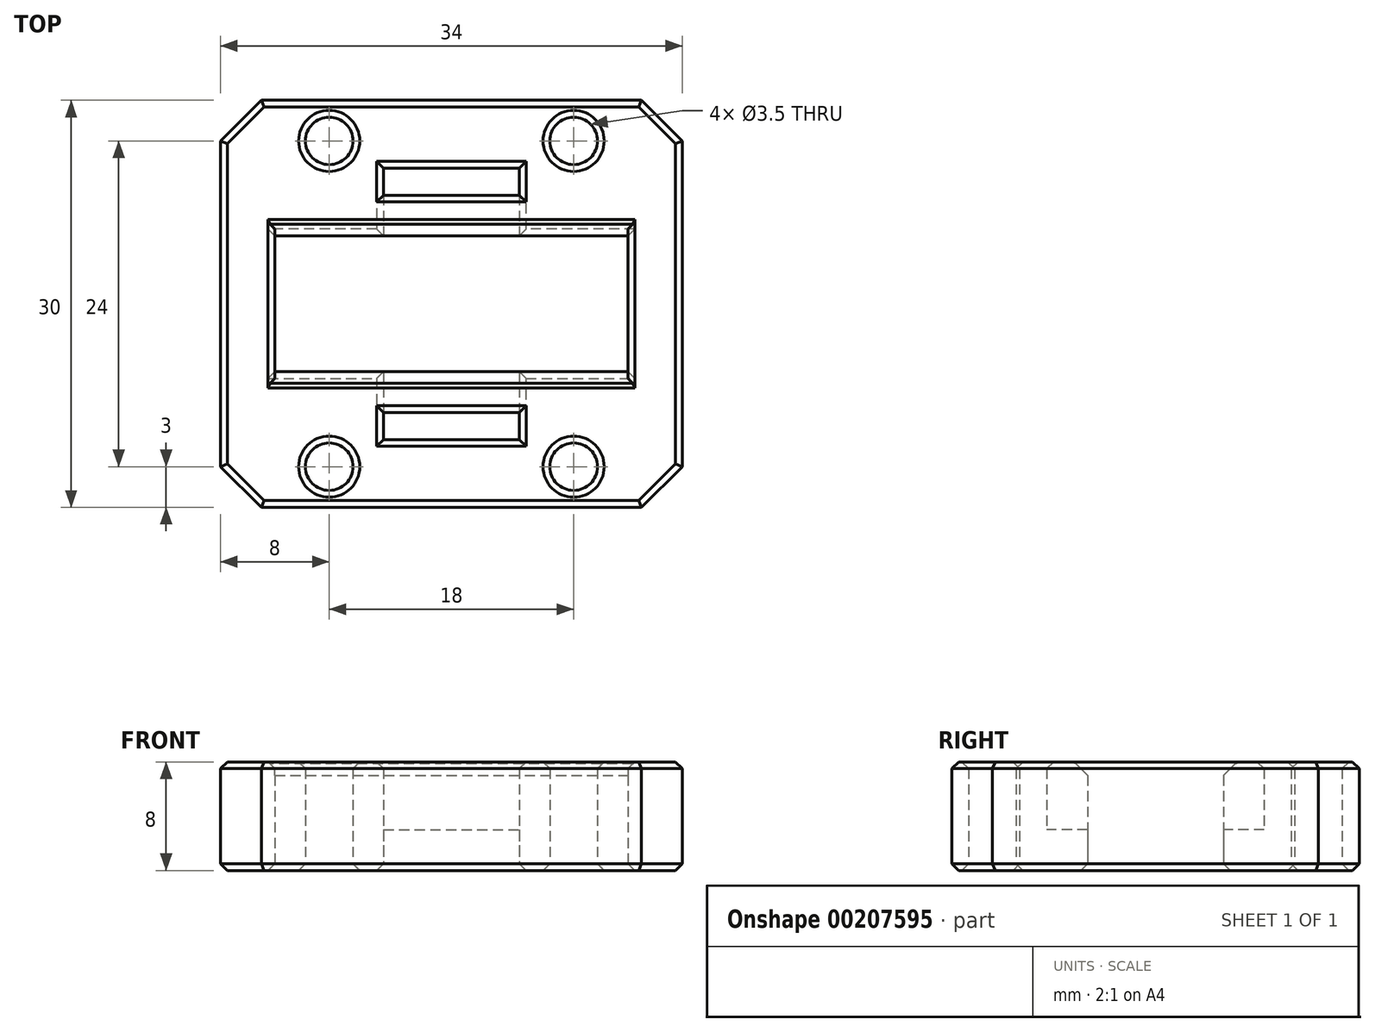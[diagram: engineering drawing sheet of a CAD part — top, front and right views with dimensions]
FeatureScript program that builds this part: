
annotation { "Feature Type Name" : "Feature", "Feature Type Description" : "" }
export const myFeature = defineFeature(function(context is Context, id is Id, definition is map)
    precondition{}
    {
        {
            var Q0;
            Q0=qCreatedBy(makeId("Top.planeOp"),FACE);
            var sketch = newSketch(context, id + "F0", { "sketchPlane" : qUnion([Q0])});
            skLineSegment(sketch, "E0.bottom", {"start": v(-17, 15) * mm, "end": v(17, 15) * mm});
            skLineSegment(sketch, "E0.top", {"start": v(-17, -15) * mm, "end": v(17, -15) * mm});
            skLineSegment(sketch, "E0.left", {"start": v(-17, 15) * mm, "end": v(-17, -15) * mm});
            skLineSegment(sketch, "E0.right", {"start": v(17, 15) * mm, "end": v(17, -15) * mm});
            skCircle(sketch, "E1", {"center": v(-9, 12) * mm, "radius": 1.75 * mm});
            skCircle(sketch, "E2", {"center": v(9, 12) * mm, "radius": 1.75 * mm});
            skCircle(sketch, "E3.MirrorC", {"center": v(-9, -12) * mm, "radius": 1.75 * mm});
            skCircle(sketch, "E4.MirrorC", {"center": v(9, -12) * mm, "radius": 1.75 * mm});
            skSolve(sketch);
        }
        {
            var Q0;
            Q0=qCreatedBy(makeId("Right.planeOp"),FACE);
            var sketch = newSketch(context, id + "F1", { "sketchPlane" : qUnion([Q0])});
            skCircle(sketch, "E5", {"center": v(0, -11) * mm, "radius": 8 * mm});
            skSolve(sketch);
        }
        {
            var Q0;
            Q0=makeQuery(id+"F0.imprint","IMPRINT",FACE,{"disambiguationData":[TD([[makeQuery(id+"F0.imprint","IMPRINT",EDGE,{"derivedFrom":sQuery(id+"F0.wireOp",EDGE,"E0.bottom")}),-1.0]])]});
            var sketch = newSketch(context, id + "F2", { "sketchPlane" : qUnion([Q0])});
            skLineSegment(sketch, "E6.bottom", {"start": v(-13, 5) * mm, "end": v(13, 5) * mm});
            skLineSegment(sketch, "E6.top", {"start": v(-13, -5) * mm, "end": v(13, -5) * mm});
            skLineSegment(sketch, "E6.left", {"start": v(-13, 5) * mm, "end": v(-13, -5) * mm});
            skLineSegment(sketch, "E6.right", {"start": v(13, 5) * mm, "end": v(13, -5) * mm});
            skLineSegment(sketch, "E7.bottom", {"start": v(-5, 10) * mm, "end": v(5, 10) * mm});
            skLineSegment(sketch, "E7.top", {"start": v(-5, 8) * mm, "end": v(5, 8) * mm});
            skLineSegment(sketch, "E7.left", {"start": v(-5, 10) * mm, "end": v(-5, 8) * mm});
            skLineSegment(sketch, "E7.right", {"start": v(5, 10) * mm, "end": v(5, 8) * mm});
            skLineSegment(sketch, "E8.MirrorCS", {"start": v(-5, -8) * mm, "end": v(5, -8) * mm});
            skLineSegment(sketch, "E9.MirrorCS", {"start": v(5, -10) * mm, "end": v(5, -8) * mm});
            skLineSegment(sketch, "E10.MirrorCS", {"start": v(-5, -10) * mm, "end": v(-5, -8) * mm});
            skLineSegment(sketch, "E11.MirrorCS", {"start": v(-5, -10) * mm, "end": v(5, -10) * mm});
            skLineSegment(sketch, "E12.left", {"start": v(-5, 8) * mm, "end": v(-5, -8) * mm});
            skLineSegment(sketch, "E12.right", {"start": v(5, 8) * mm, "end": v(5, -8) * mm});
            skSolve(sketch);
        }
        {
            var Q0;
            Q0=makeQuery(id+"F0.imprint","IMPRINT",FACE,{"disambiguationData":[TD([[makeQuery(id+"F0.imprint","IMPRINT",EDGE,{"derivedFrom":sQuery(id+"F0.wireOp",EDGE,"E0.bottom")}),-1.0]])]});
            extrude(context, id + "F3", {"entities" : qUnion([Q0]), "depth" : 8 * mm});
        }
        {
            var Q0;
            Q0=makeQuery(id+"F2.imprint","IMPRINT",FACE,{"disambiguationData":[TD([[makeQuery(id+"F2.imprint","IMPRINT",EDGE,{"derivedFrom":sQuery(id+"F2.wireOp",EDGE,"E9.MirrorCS")}),1.0]])]});
            var Q1;
            Q1=makeQuery(id+"F2.imprint","IMPRINT",FACE,{"disambiguationData":[TD([[makeQuery(id+"F2.imprint","IMPRINT",EDGE,{"derivedFrom":sQuery(id+"F2.wireOp",EDGE,"E7.bottom")}),-1.0]])]});
            var Q2;
            {var subQ0=sQuery(id+"F2.wireOp",EDGE,"E6.right");Q2=makeQuery(id+"F2.imprint","IMPRINT",FACE,{"disambiguationData":[TD([[makeQuery(id+"F2.imprint","IMPRINT",EDGE,{"derivedFrom":subQ0}),-1.0]])]});}
            var Q3;
            {var subQ0=sQuery(id+"F2.wireOp",EDGE,"E12.left");var subQ1=sQuery(id+"F2.wireOp",EDGE,"E6.bottom");var subQ2=makeQuery(id+"F2.imprint","INTERSECT",VERTEX,{"derivedFrom":[subQ1,subQ0]});Q3=makeQuery(id+"F2.imprint","IMPRINT",FACE,{"disambiguationData":[TD([[makeQuery(id+"F2.imprint","IMPRINT",EDGE,{"disambiguationData":[TD([[subQ2,-1.0]])],"derivedFrom":subQ1}),-1.0]])]});}
            var Q4;
            {var subQ0=sQuery(id+"F2.wireOp",EDGE,"E6.left");Q4=makeQuery(id+"F2.imprint","IMPRINT",FACE,{"disambiguationData":[TD([[makeQuery(id+"F2.imprint","IMPRINT",EDGE,{"derivedFrom":subQ0}),1.0]])]});}
            extrude(context, id + "F4", {"entities" : qUnion([Q0, Q1, Q2, Q3, Q4]), "operationType" : NewBodyOperationType.REMOVE, "depth" : 25 * mm});
        }
        {
            var Q0;
            {var subQ5=sQuery(id+"F2.wireOp",EDGE,"E8.MirrorCS");Q0=makeQuery(id+"F2.imprint","IMPRINT",FACE,{"disambiguationData":[TD([[makeQuery(id+"F2.imprint","IMPRINT",EDGE,{"derivedFrom":subQ5}),1.0]])]});}
            var Q1;
            {var subQ5=sQuery(id+"F2.wireOp",EDGE,"E7.top");Q1=makeQuery(id+"F2.imprint","IMPRINT",FACE,{"disambiguationData":[TD([[makeQuery(id+"F2.imprint","IMPRINT",EDGE,{"derivedFrom":subQ5}),-1.0]])]});}
            extrude(context, id + "F5", {"entities" : qUnion([Q0, Q1]), "operationType" : NewBodyOperationType.REMOVE, "depth" : 3 * mm});
        }
        {
            var Q0;
            Q0=makeQuery(id+"F4.boolean.opBoolean","INTERSECT",EDGE,{"derivedFrom":[makeQuery(id+"F3.opExtrude","CAP_FACE",FACE,{"disambiguationData":[OSD([sQuery(id+"F0.wireOp",EDGE,"E0.bottom"),sQuery(id+"F0.wireOp",EDGE,"E0.top"),sQuery(id+"F0.wireOp",EDGE,"E0.left"),sQuery(id+"F0.wireOp",EDGE,"E0.right"),sQuery(id+"F0.wireOp",EDGE,"E1"),sQuery(id+"F0.wireOp",EDGE,"E2"),sQuery(id+"F0.wireOp",EDGE,"E3.MirrorC"),sQuery(id+"F0.wireOp",EDGE,"E4.MirrorC")])],"isStart":false}),makeQuery(id+"F4.opExtrude","SWEPT_FACE",FACE,{"disambiguationData":[OSD([sQuery(id+"F2.wireOp",EDGE,"E6.top")])]})]});
            var Q1;
            Q1=makeQuery(id+"F4.boolean.opBoolean","INTERSECT",EDGE,{"derivedFrom":[makeQuery(id+"F3.opExtrude","CAP_FACE",FACE,{"disambiguationData":[OSD([sQuery(id+"F0.wireOp",EDGE,"E0.bottom"),sQuery(id+"F0.wireOp",EDGE,"E0.top"),sQuery(id+"F0.wireOp",EDGE,"E0.left"),sQuery(id+"F0.wireOp",EDGE,"E0.right"),sQuery(id+"F0.wireOp",EDGE,"E1"),sQuery(id+"F0.wireOp",EDGE,"E2"),sQuery(id+"F0.wireOp",EDGE,"E3.MirrorC"),sQuery(id+"F0.wireOp",EDGE,"E4.MirrorC")])],"isStart":false}),makeQuery(id+"F4.opExtrude","SWEPT_FACE",FACE,{"disambiguationData":[OSD([sQuery(id+"F2.wireOp",EDGE,"E6.bottom")])]})]});
            var Q2;
            Q2=makeQuery(id+"F5.boolean.opBoolean","COPY",EDGE,{"derivedFrom":makeQuery(id+"F5.opExtrude","CAP_EDGE",EDGE,{"disambiguationData":[OSD([sQuery(id+"F2.wireOp",EDGE,"E8.MirrorCS")])],"isStart":false})});
            var Q3;
            Q3=makeQuery(id+"F5.boolean.opBoolean","COPY",EDGE,{"derivedFrom":makeQuery(id+"F5.opExtrude","CAP_EDGE",EDGE,{"disambiguationData":[OSD([sQuery(id+"F2.wireOp",EDGE,"E7.top")])],"isStart":false})});
            chamfer(context, id + "F6", {"entities" : qUnion([Q0, Q1, Q2, Q3]), "width" : 1 * mm, "tangentPropagation" : true});
        }
        {
            var Q0;
            Q0=makeQuery(id+"F3.opExtrude","SWEPT_EDGE",EDGE,{"disambiguationData":[OSD([sQuery(id+"F0.wireOp",EDGE,"E0.bottom"),sQuery(id+"F0.wireOp",EDGE,"E0.left")])]});
            var Q1;
            Q1=makeQuery(id+"F3.opExtrude","SWEPT_EDGE",EDGE,{"disambiguationData":[OSD([sQuery(id+"F0.wireOp",EDGE,"E0.bottom"),sQuery(id+"F0.wireOp",EDGE,"E0.right")])]});
            var Q2;
            Q2=makeQuery(id+"F3.opExtrude","SWEPT_EDGE",EDGE,{"disambiguationData":[OSD([sQuery(id+"F0.wireOp",EDGE,"E0.top"),sQuery(id+"F0.wireOp",EDGE,"E0.right")])]});
            var Q3;
            Q3=makeQuery(id+"F3.opExtrude","SWEPT_EDGE",EDGE,{"disambiguationData":[OSD([sQuery(id+"F0.wireOp",EDGE,"E0.top"),sQuery(id+"F0.wireOp",EDGE,"E0.left")])]});
            chamfer(context, id + "F7", {"entities" : qUnion([Q0, Q1, Q2, Q3]), "width" : 3 * mm, "tangentPropagation" : true});
        }
        {
            var Q0;
            Q0=makeQuery(id+"F3.opExtrude","CAP_FACE",FACE,{"disambiguationData":[OSD([sQuery(id+"F0.wireOp",EDGE,"E0.bottom"),sQuery(id+"F0.wireOp",EDGE,"E0.top"),sQuery(id+"F0.wireOp",EDGE,"E0.left"),sQuery(id+"F0.wireOp",EDGE,"E0.right"),sQuery(id+"F0.wireOp",EDGE,"E1"),sQuery(id+"F0.wireOp",EDGE,"E2"),sQuery(id+"F0.wireOp",EDGE,"E3.MirrorC"),sQuery(id+"F0.wireOp",EDGE,"E4.MirrorC")])],"isStart":false});
            var Q1;
            Q1=makeQuery(id+"F3.opExtrude","CAP_FACE",FACE,{"disambiguationData":[OSD([sQuery(id+"F0.wireOp",EDGE,"E0.bottom"),sQuery(id+"F0.wireOp",EDGE,"E0.top"),sQuery(id+"F0.wireOp",EDGE,"E0.left"),sQuery(id+"F0.wireOp",EDGE,"E0.right"),sQuery(id+"F0.wireOp",EDGE,"E1"),sQuery(id+"F0.wireOp",EDGE,"E2"),sQuery(id+"F0.wireOp",EDGE,"E3.MirrorC"),sQuery(id+"F0.wireOp",EDGE,"E4.MirrorC")])],"isStart":true});
            chamfer(context, id + "F8", {"entities" : qUnion([Q0, Q1]), "width" : .5 * mm, "tangentPropagation" : true});
        }
    });
